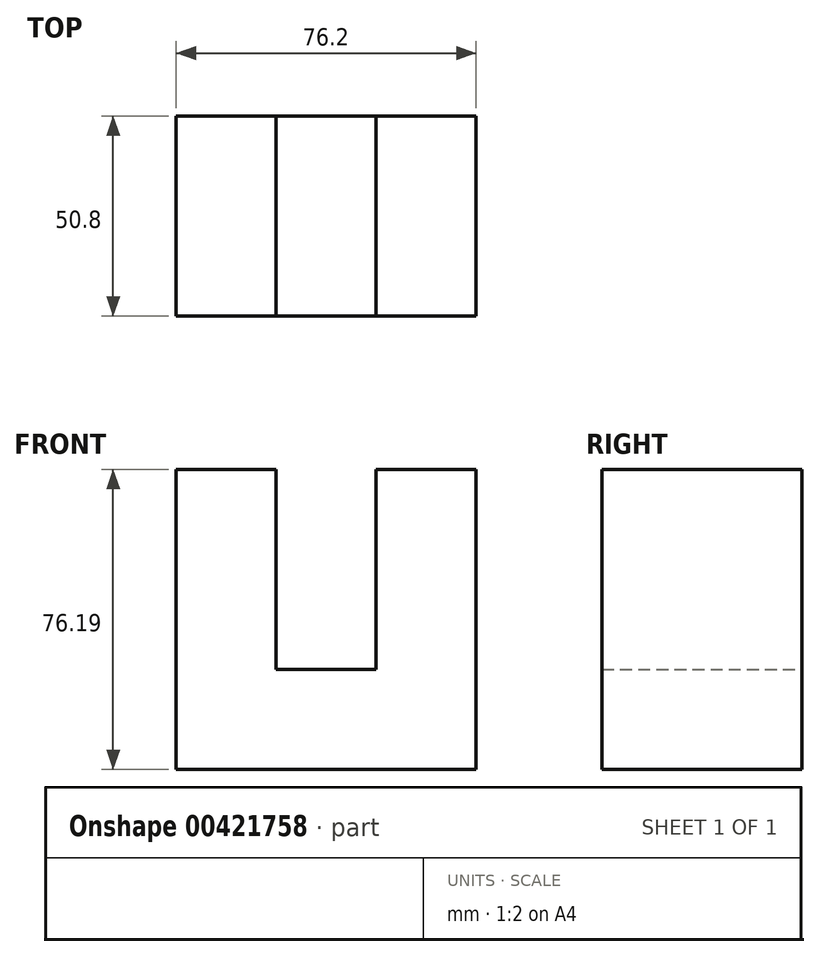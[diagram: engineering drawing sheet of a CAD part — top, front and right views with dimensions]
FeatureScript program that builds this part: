
annotation { "Feature Type Name" : "Feature", "Feature Type Description" : "" }
export const myFeature = defineFeature(function(context is Context, id is Id, definition is map)
    precondition{}
    {
        {
            var Q0;
            Q0=qCreatedBy(makeId("Front.planeOp"),FACE);
            var sketch = newSketch(context, id + "F0", { "sketchPlane" : qUnion([Q0])});
            skLineSegment(sketch, "E0", {"start": v(0, 0) * mm, "end": v(0, 76.2) * mm});
            skLineSegment(sketch, "E1", {"start": v(0, 76.2) * mm, "end": v(25.4, 76.2) * mm});
            skLineSegment(sketch, "E2", {"start": v(25.4, 76.2) * mm, "end": v(25.4, 25.4) * mm});
            skLineSegment(sketch, "E3", {"start": v(25.4, 25.4) * mm, "end": v(50.8, 25.4) * mm});
            skLineSegment(sketch, "E4", {"start": v(50.8, 25.4) * mm, "end": v(50.8, 76.2) * mm});
            skLineSegment(sketch, "E5", {"start": v(50.8, 76.2) * mm, "end": v(76.2, 76.2) * mm});
            skLineSegment(sketch, "E6", {"start": v(76.2, 76.2) * mm, "end": v(76.2, 25.4) * mm});
            skLineSegment(sketch, "E7", {"start": v(76.2, 25.4) * mm, "end": v(76.2, 0) * mm});
            skLineSegment(sketch, "E8", {"start": v(76.2, 0) * mm, "end": v(0, 0) * mm});
            skSolve(sketch);
        }
        {
            var Q0;
            Q0 = qSketchRegion(id + "F0", true);
            extrude(context, id + "F1", {"entities" : qUnion([Q0]), "depth" : 50.8 * mm});
        }
    });
